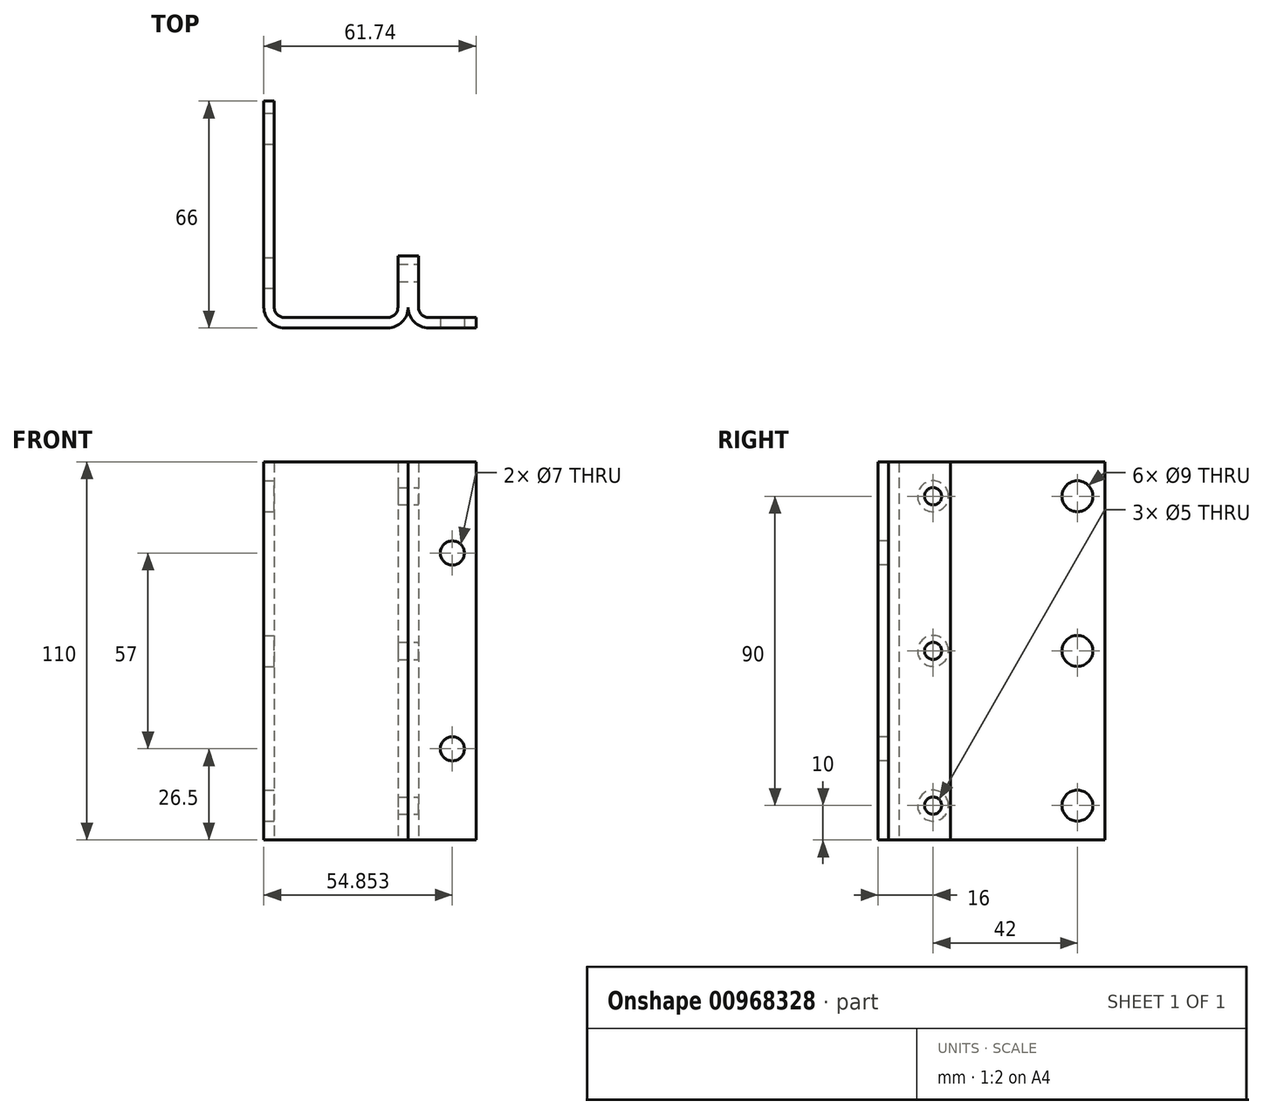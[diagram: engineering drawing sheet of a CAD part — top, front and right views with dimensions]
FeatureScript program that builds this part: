
annotation { "Feature Type Name" : "Feature", "Feature Type Description" : "" }
export const myFeature = defineFeature(function(context is Context, id is Id, definition is map)
    precondition{}
    {
        {
            var Q0;
            Q0=qCreatedBy(makeId("Top.planeOp"),FACE);
            var sketch = newSketch(context, id + "F0", { "sketchPlane" : qUnion([Q0])});
            skLineSegment(sketch, "E0", {"start": v(-42, 45) * mm, "end": v(-42, -15) * mm});
            skLineSegment(sketch, "E1", {"start": v(-42, 45) * mm, "end": v(-39, 45) * mm});
            skLineSegment(sketch, "E2", {"start": v(-39, 45) * mm, "end": v(-39, -15) * mm});
            skLineSegment(sketch, "E3", {"start": v(-3, -15) * mm, "end": v(-3, 0) * mm});
            skLineSegment(sketch, "E4", {"start": v(-3, 0) * mm, "end": v(3, 0) * mm});
            skLineSegment(sketch, "E5", {"start": v(3, 0) * mm, "end": v(3, -15) * mm});
            skLineSegment(sketch, "E6", {"start": v(-36, -18) * mm, "end": v(-6, -18) * mm});
            skLineSegment(sketch, "E7", {"start": v(-36, -21) * mm, "end": v(-6, -21) * mm});
            skLineSegment(sketch, "E8", {"start": v(6, -18) * mm, "end": v(19.74, -18) * mm});
            skLineSegment(sketch, "E9", {"start": v(6, -21) * mm, "end": v(19.74, -21) * mm});
            skLineSegment(sketch, "E10", {"start": v(19.74, -21) * mm, "end": v(19.74, -18) * mm});
            skArc(sketch, "E11", {"start": v(-39, -15) * mm, "mid": v(-38.12, -17.12) * mm, "end": v(-36, -18) * mm});
            skArc(sketch, "E12", {"start": v(-42, -15) * mm, "mid": v(-40.24, -19.24) * mm, "end": v(-36, -21) * mm});
            skArc(sketch, "E13", {"start": v(-6, -18) * mm, "mid": v(-3.88, -17.12) * mm, "end": v(-3, -15) * mm});
            skPoint(sketch, "E14", {"position": v(0, -15) * mm});
            skArc(sketch, "E15", {"start": v(-6, -21) * mm, "mid": v(-1.76, -19.24) * mm, "end": v(0, -15) * mm});
            skArc(sketch, "E16", {"start": v(3, -15) * mm, "mid": v(3.88, -17.12) * mm, "end": v(6, -18) * mm});
            skArc(sketch, "E17", {"start": v(0, -15) * mm, "mid": v(1.76, -19.24) * mm, "end": v(6, -21) * mm});
            skSolve(sketch);
        }
        {
            var Q0;
            Q0 = qSketchRegion(id + "F0", true);
            extrude(context, id + "F1", {"entities" : qUnion([Q0]), "depth" : 55 * mm, "offsetDistance" : 25 * mm, "hasSecondDirection" : true, "secondDirectionOppositeDirection" : true, "secondDirectionDepth" : 55 * mm});
        }
        {
            var Q0;
            Q0=makeQuery(id+"F1.opExtrude","SWEPT_FACE",FACE,{"disambiguationData":[OSD([sQuery(id+"F0.wireOp",EDGE,"E5")])]});
            var sketch = newSketch(context, id + "F2", { "sketchPlane" : qUnion([Q0])});
            skCircle(sketch, "E18", {"center": v(-5, 45) * mm, "radius": 2.5 * mm});
            skCircle(sketch, "E19", {"center": v(-5, 0) * mm, "radius": 2.5 * mm});
            skCircle(sketch, "E20", {"center": v(-5, -45) * mm, "radius": 2.5 * mm});
            skSolve(sketch);
        }
        {
            var Q0;
            Q0 = qSketchRegion(id + "F2", true);
            var Q1;
            Q1=sQuery(id+"F2.wireOp",EDGE,"E18");
            var Q2;
            Q2=sQuery(id+"F2.wireOp",EDGE,"E19");
            var Q3;
            Q3=sQuery(id+"F2.wireOp",EDGE,"E20");
            extrude(context, id + "F3", {"entities" : qUnion([Q0]), "operationType" : NewBodyOperationType.REMOVE, "surfaceEntities" : qUnion([Q1, Q2, Q3]), "endBound" : BoundingType.THROUGH_ALL, "oppositeDirection" : true, "depth" : 25 * mm, "offsetDistance" : 25 * mm});
        }
        {
            var Q0;
            Q0=makeQuery(id+"F1.opExtrude","SWEPT_FACE",FACE,{"disambiguationData":[OSD([sQuery(id+"F0.wireOp",EDGE,"E2")])]});
            var sketch = newSketch(context, id + "F4", { "sketchPlane" : qUnion([Q0])});
            skCircle(sketch, "E21", {"center": v(-5, 45) * mm, "radius": 4.5 * mm});
            skCircle(sketch, "E22", {"center": v(-5, 0) * mm, "radius": 4.5 * mm});
            skCircle(sketch, "E23", {"center": v(-5, -45) * mm, "radius": 4.5 * mm});
            skSolve(sketch);
        }
        {
            var Q0;
            Q0 = qSketchRegion(id + "F4", true);
            extrude(context, id + "F5", {"entities" : qUnion([Q0]), "operationType" : NewBodyOperationType.REMOVE, "oppositeDirection" : true, "depth" : 3 * mm, "offsetDistance" : 25 * mm});
        }
        {
            var Q0;
            Q0=makeQuery(id+"F1.opExtrude","SWEPT_FACE",FACE,{"disambiguationData":[OSD([sQuery(id+"F0.wireOp",EDGE,"E2")])]});
            var sketch = newSketch(context, id + "F6", { "sketchPlane" : qUnion([Q0])});
            skCircle(sketch, "E24", {"center": v(37, 0) * mm, "radius": 4.5 * mm});
            skCircle(sketch, "E25", {"center": v(37, -45) * mm, "radius": 4.5 * mm});
            skCircle(sketch, "E26", {"center": v(37, 45) * mm, "radius": 4.5 * mm});
            skSolve(sketch);
        }
        {
            var Q0;
            Q0 = qSketchRegion(id + "F6", true);
            extrude(context, id + "F7", {"entities" : qUnion([Q0]), "operationType" : NewBodyOperationType.REMOVE, "oppositeDirection" : true, "depth" : 3 * mm, "offsetDistance" : 25 * mm});
        }
        {
            var Q0;
            Q0=makeQuery(id+"F1.opExtrude","SWEPT_FACE",FACE,{"disambiguationData":[OSD([sQuery(id+"F0.wireOp",EDGE,"E9")])]});
            var sketch = newSketch(context, id + "F8", { "sketchPlane" : qUnion([Q0])});
            skCircle(sketch, "E27", {"center": v(12.85, 28.5) * mm, "radius": 3.5 * mm});
            skCircle(sketch, "E28", {"center": v(12.85, -28.5) * mm, "radius": 3.5 * mm});
            skSolve(sketch);
        }
        {
            var Q0;
            Q0 = qSketchRegion(id + "F8", true);
            extrude(context, id + "F9", {"entities" : qUnion([Q0]), "operationType" : NewBodyOperationType.REMOVE, "oppositeDirection" : true, "depth" : 3 * mm, "offsetDistance" : 25 * mm});
        }
    });
